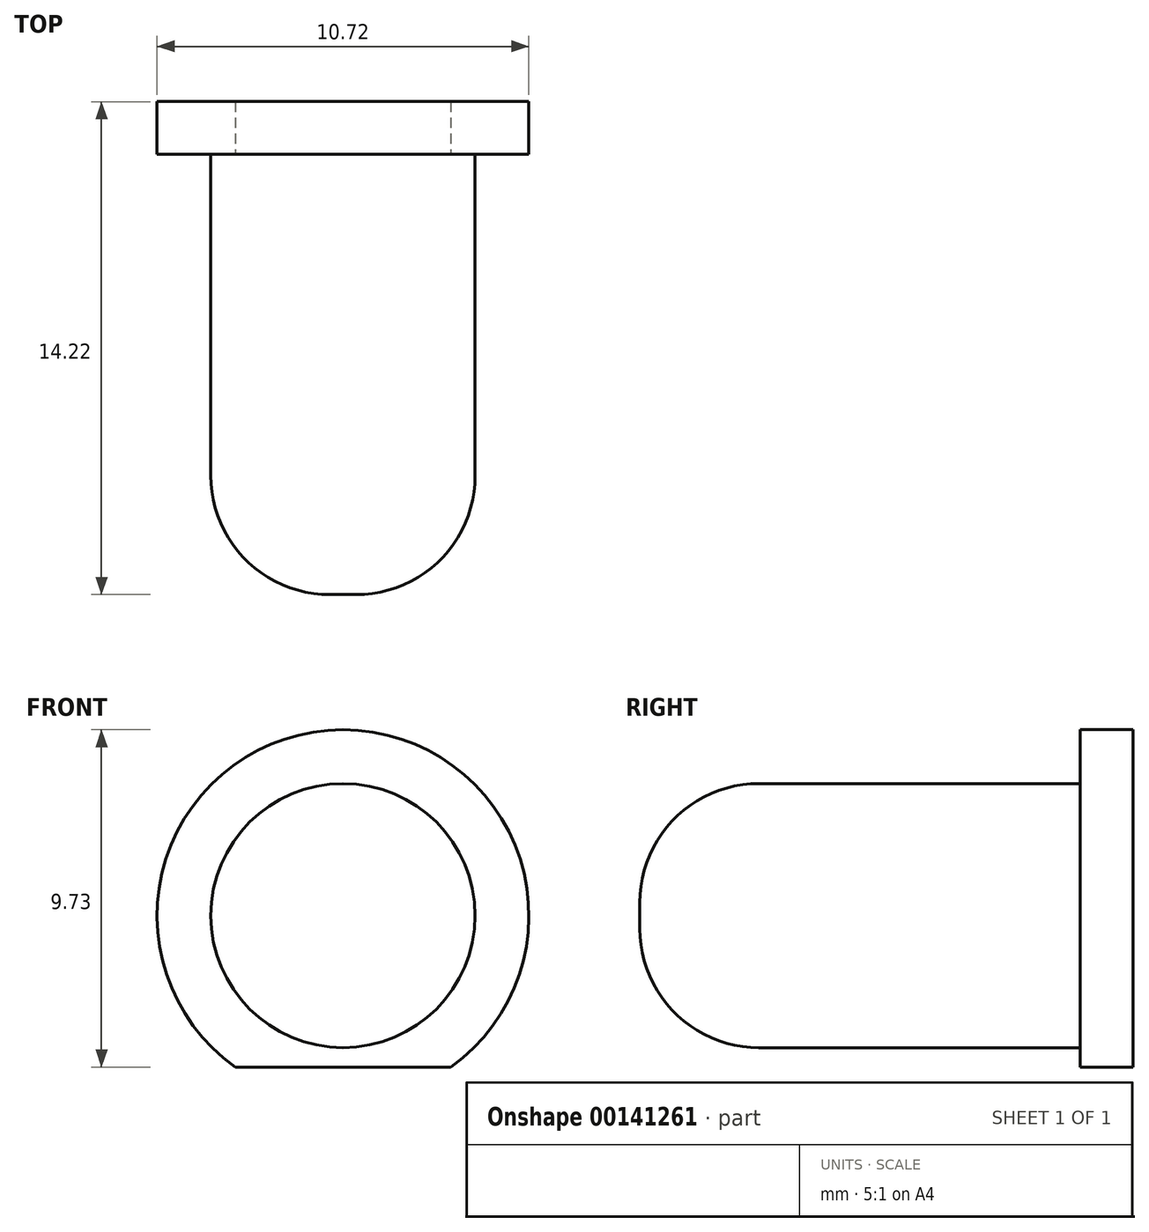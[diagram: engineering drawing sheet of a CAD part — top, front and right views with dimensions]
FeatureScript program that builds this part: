
annotation { "Feature Type Name" : "Feature", "Feature Type Description" : "" }
export const myFeature = defineFeature(function(context is Context, id is Id, definition is map)
    precondition{}
    {
        {
            var Q0;
            Q0=qCreatedBy(makeId("Front.planeOp"),FACE);
            var sketch = newSketch(context, id + "F0", { "sketchPlane" : qUnion([Q0])});
            skCircle(sketch, "E0", {"center": v(0, 0) * mm, "radius": 3.8 * mm});
            skSolve(sketch);
        }
        {
            var Q0;
            Q0 = qSketchRegion(id + "F0", true);
            extrude(context, id + "F1", {"entities" : qUnion([Q0]), "depth" : 12.7 * mm});
        }
        {
            var Q0;
            Q0=makeQuery(id+"F1.opExtrude","CAP_EDGE",EDGE,{"disambiguationData":[OSD([sQuery(id+"F0.wireOp",EDGE,"E0")])],"isStart":false});
            fillet(context, id + "F2", {"entities" : qUnion([Q0]), "radius" : 3.43 * mm, "tangentPropagation" : true, "allowEdgeOverflow" : false});
        }
        {
            var Q0;
            Q0=makeQuery(id+"F1.opExtrude","CAP_FACE",FACE,{"disambiguationData":[OSD([sQuery(id+"F0.wireOp",EDGE,"E0")])],"isStart":true});
            var sketch = newSketch(context, id + "F3", { "sketchPlane" : qUnion([Q0])});
            skArc(sketch, "E1", {"start": v(3.1, -4.37) * mm, "mid": v(0, 5.36) * mm, "end": v(-3.1, -4.37) * mm});
            skLineSegment(sketch, "E2", {"start": v(3.1, -4.37) * mm, "end": v(-3.1, -4.37) * mm});
            skSolve(sketch);
        }
        {
            var Q0;
            Q0 = qSketchRegion(id + "F3", true);
            extrude(context, id + "F4", {"entities" : qUnion([Q0]), "operationType" : NewBodyOperationType.ADD, "depth" : 1.52 * mm});
        }
    });
